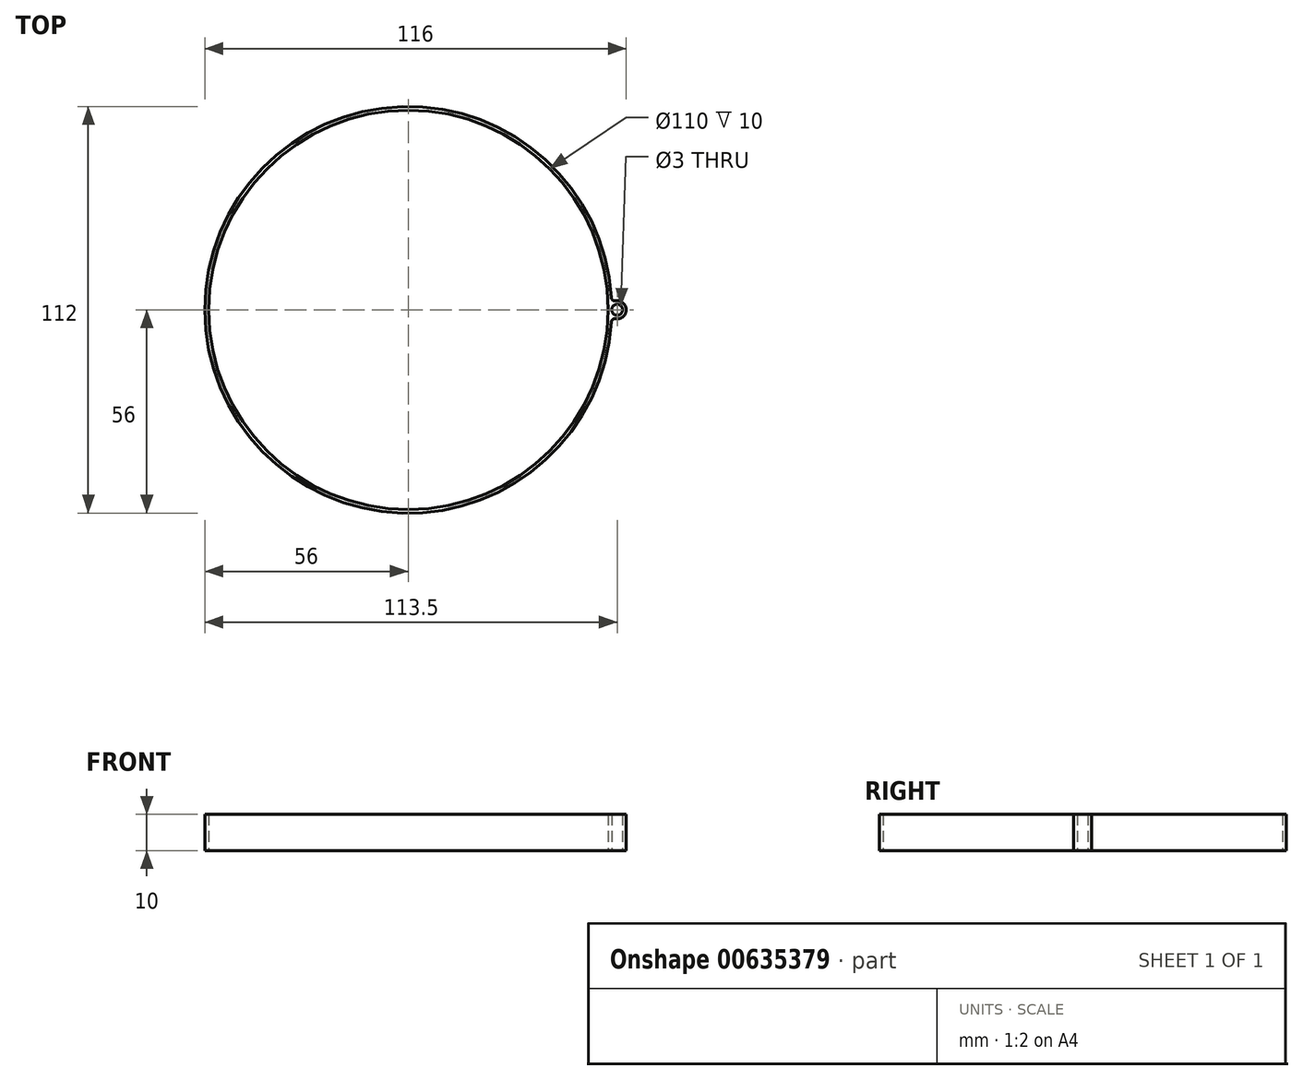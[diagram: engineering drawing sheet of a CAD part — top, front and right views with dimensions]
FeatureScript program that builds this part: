
annotation { "Feature Type Name" : "Feature", "Feature Type Description" : "" }
export const myFeature = defineFeature(function(context is Context, id is Id, definition is map)
    precondition{}
    {
        {
            var Q0;
            Q0=qCreatedBy(makeId("Front.planeOp"),FACE);
            var sketch = newSketch(context, id + "F0", { "sketchPlane" : qUnion([Q0])});
            skLineSegment(sketch, "E0.bottom", {"start": v(55, 0) * mm, "end": v(56, 0) * mm});
            skLineSegment(sketch, "E0.top", {"start": v(55, 10) * mm, "end": v(56, 10) * mm});
            skLineSegment(sketch, "E0.left", {"start": v(55, 0) * mm, "end": v(55, 10) * mm});
            skLineSegment(sketch, "E0.right", {"start": v(56, 0) * mm, "end": v(56, 10) * mm});
            skLineSegment(sketch, "E1", {"start": v(0, 0) * mm, "end": v(0, 50.15) * mm, "construction": true});
            skSolve(sketch);
        }
        {
            var Q0;
            Q0=makeQuery(id+"F0.imprint","IMPRINT",FACE,{"disambiguationData":[TD([[makeQuery(id+"F0.imprint","IMPRINT",EDGE,{"derivedFrom":sQuery(id+"F0.wireOp",EDGE,"E0.bottom")}),1.0]])]});
            var Q1;
            Q1=sQuery(id+"F0.wireOp",EDGE,"E0.right");
            var Q2;
            Q2=sQuery(id+"F0.wireOp",EDGE,"E1");
            revolve(context, id + "F1", {"entities" : qUnion([Q0]), "surfaceEntities" : qUnion([Q1]), "axis" : qUnion([Q2]), "revolveType" : RevolveType.FULL, "surfaceOperationType" : NewSurfaceOperationType.NEW});
        }
        {
            var Q0;
            Q0=qCreatedBy(makeId("Top.planeOp"),FACE);
            var sketch = newSketch(context, id + "F2", { "sketchPlane" : qUnion([Q0])});
            skCircle(sketch, "E2", {"center": v(57.5, 0) * mm, "radius": 1.5 * mm});
            skArc(sketch, "E3", {"start": v(57.07, -2.46) * mm, "mid": v(60, 0) * mm, "end": v(57.07, 2.46) * mm});
            skArc(sketch, "E4.0.0", {"start": v(55.9, -3.39) * mm, "mid": v(56, 0) * mm, "end": v(55.9, 3.39) * mm, "construction": true});
            skArc(sketch, "E5", {"start": v(55.9, 3.39) * mm, "mid": v(56.28, 2.66) * mm, "end": v(57.07, 2.46) * mm});
            skArc(sketch, "E6.filletArc", {"start": v(57.07, -2.46) * mm, "mid": v(56.28, -2.66) * mm, "end": v(55.9, -3.39) * mm});
            skArc(sketch, "E7.0", {"start": v(55.4, -3.36) * mm, "mid": v(55.5, 0) * mm, "end": v(55.4, 3.36) * mm});
            skCircle(sketch, "E8.0", {"center": v(0, 0) * mm, "radius": 51 * mm});
            skLineSegment(sketch, "E9", {"start": v(55.4, 3.36) * mm, "end": v(55.9, 3.39) * mm});
            skLineSegment(sketch, "E10", {"start": v(55.4, -3.36) * mm, "end": v(55.9, -3.39) * mm});
            skSolve(sketch);
        }
        {
            var Q0;
            {var subQ2=sQuery(id+"F2.wireOp",EDGE,"E2");Q0=makeQuery(id+"F2.imprint","IMPRINT",FACE,{"disambiguationData":[TD([[makeQuery(id+"F2.imprint","IMPRINT",EDGE,{"derivedFrom":subQ2}),-1.0]])]});}
            extrude(context, id + "F3", {"entities" : qUnion([Q0]), "operationType" : NewBodyOperationType.ADD, "depth" : 10 * mm, "offsetDistance" : 25 * mm});
        }
    });
